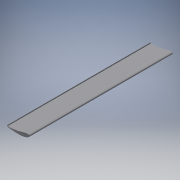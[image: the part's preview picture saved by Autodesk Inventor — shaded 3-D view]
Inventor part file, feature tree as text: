
AUTODESK INVENTOR PART (.ipt)
format: ipt  version: 2018.2 (Build 222227000, 227)  size: 157,184 bytes
history: native  units: mm
features: other x4, extrude x2, sketch x2, mirror x1, projected_geometry x1
ambient origin geometry x8: Origin, YZ Plane, XZ Plane, XY Plane, X Axis, Y Axis, Z Axis, Center Point
bodies: Body1 (feature_tree)
feature tree (10):
  other  "main frap.ipt"
  extrude  "押し出し2"  Depth=4.0mm
  mirror  "ミラー2"
  extrude  "押し出し3"  Depth=285.0mm TaperAngle=0.0deg
  other  "ソリッド1::main frap.ipt"
  other  "TaggingFeature1"
  sketch  "スケッチ2"
  projected_geometry  "投影ループ2"
  sketch  "スケッチ3"
  other  "ソリッド1"
